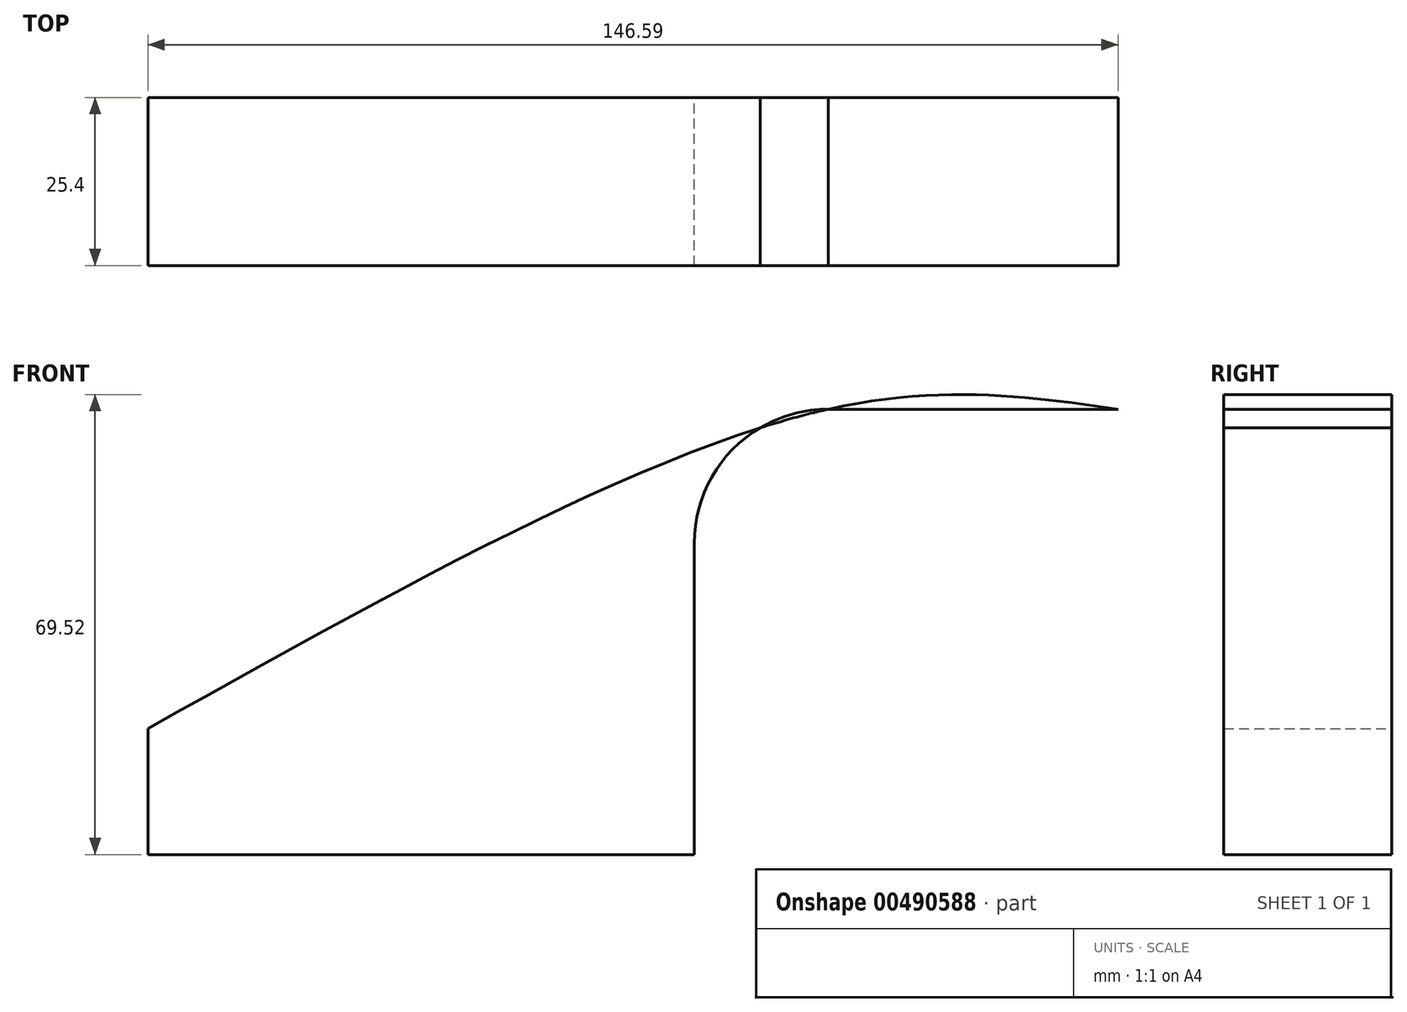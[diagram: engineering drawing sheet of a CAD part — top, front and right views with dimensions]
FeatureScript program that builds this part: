
annotation { "Feature Type Name" : "Feature", "Feature Type Description" : "" }
export const myFeature = defineFeature(function(context is Context, id is Id, definition is map)
    precondition{}
    {
        {
            var Q0;
            Q0=qCreatedBy(makeId("Front.planeOp"),FACE);
            var sketch = newSketch(context, id + "F0", { "sketchPlane" : qUnion([Q0])});
            skLineSegment(sketch, "E0.bottom", {"start": v(-41.28, -9.53) * mm, "end": v(41.28, -9.53) * mm});
            skLineSegment(sketch, "E0.top", {"start": v(-41.28, 9.52) * mm, "end": v(41.28, 9.52) * mm});
            skLineSegment(sketch, "E0.left", {"start": v(-41.28, -9.53) * mm, "end": v(-41.28, 9.52) * mm});
            skLineSegment(sketch, "E0.right", {"start": v(41.28, -9.53) * mm, "end": v(41.28, 9.52) * mm});
            skPoint(sketch, "E0.middle", {"position": v(0, 0) * mm});
            skLineSegment(sketch, "E1", {"start": v(41.27, 9.52) * mm, "end": v(41.27, 37.5) * mm});
            skArc(sketch, "E2", {"start": v(41.28, 37.5) * mm, "mid": v(47.21, 51.84) * mm, "end": v(61.55, 57.78) * mm});
            skLineSegment(sketch, "E3", {"start": v(61.55, 57.78) * mm, "end": v(105.31, 57.78) * mm});
            skFitSpline(sketch, "E4", {"points": [v(-41.28, 9.53) * mm, v(61.55, 57.78) * mm, v(105.31, 57.78) * mm], "startDerivative": vector(182.81, 102.34) * mm, "endDerivative": vector(104.23, -14.98) * mm});
            skSolve(sketch);
        }
        {
            var Q0;
            Q0 = qSketchRegion(id + "F0", true);
            extrude(context, id + "F1", {"entities" : qUnion([Q0]), "depth" : 25.4 * mm});
        }
    });
